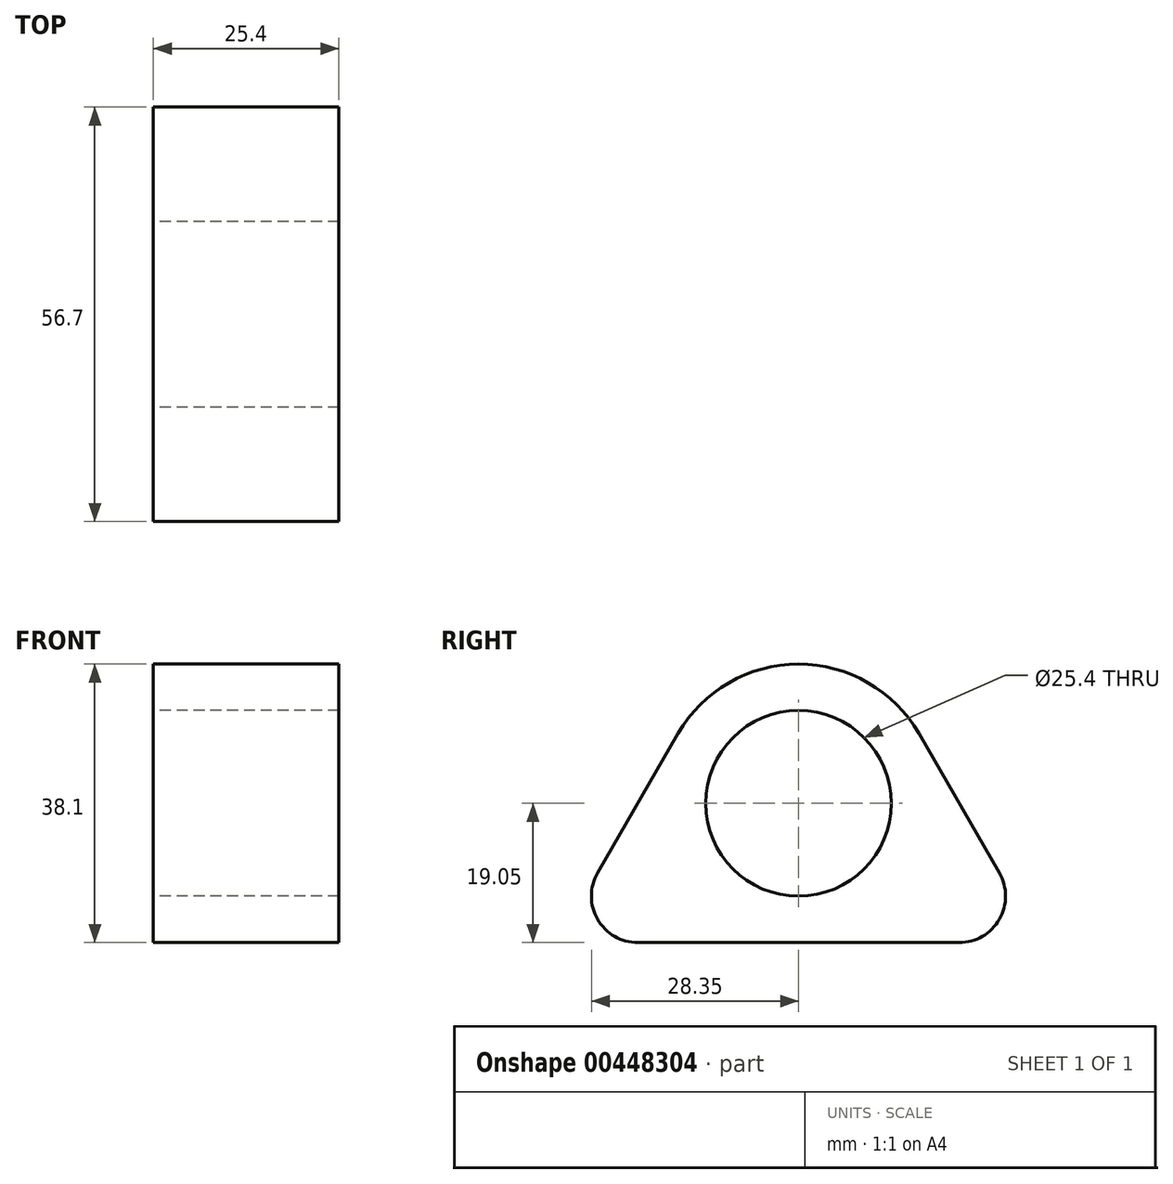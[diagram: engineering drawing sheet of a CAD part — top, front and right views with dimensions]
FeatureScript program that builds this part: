
annotation { "Feature Type Name" : "Feature", "Feature Type Description" : "" }
export const myFeature = defineFeature(function(context is Context, id is Id, definition is map)
    precondition{}
    {
        {
            var Q0;
            Q0=qCreatedBy(makeId("Right.planeOp"),FACE);
            var sketch = newSketch(context, id + "F0", { "sketchPlane" : qUnion([Q0])});
            skCircle(sketch, "E0", {"center": v(0, 0) * mm, "radius": 12.7 * mm});
            skCircle(sketch, "E1", {"center": v(0, 0) * mm, "radius": 19.05 * mm});
            skLineSegment(sketch, "E2", {"start": v(0, -19.05) * mm, "end": v(22, -19.05) * mm});
            skLineSegment(sketch, "E3", {"start": v(27.5, -9.52) * mm, "end": v(16.5, 9.53) * mm});
            skPoint(sketch, "E4.visualSharp", {"position": v(33, -19.05) * mm});
            skArc(sketch, "E4.filletArc", {"start": v(22, -19.05) * mm, "mid": v(27.5, -15.88) * mm, "end": v(27.5, -9.52) * mm});
            skLineSegment(sketch, "E5.MirrorCS", {"start": v(-27.5, -9.52) * mm, "end": v(-16.5, 9.53) * mm});
            skArc(sketch, "E6.MirrorCS", {"start": v(-22, -19.05) * mm, "mid": v(-27.5, -15.88) * mm, "end": v(-27.5, -9.52) * mm});
            skLineSegment(sketch, "E7.MirrorCS", {"start": v(0, -19.05) * mm, "end": v(-22, -19.05) * mm});
            skSolve(sketch);
        }
        {
            var Q0;
            Q0=makeQuery(id+"F0.imprint","IMPRINT",FACE,{"disambiguationData":[TD([[makeQuery(id+"F0.imprint","IMPRINT",EDGE,{"derivedFrom":sQuery(id+"F0.wireOp",EDGE,"E0")}),-1.0]])]});
            var Q1;
            {var subQ0=sQuery(id+"F0.wireOp",EDGE,"E2");Q1=makeQuery(id+"F0.imprint","IMPRINT",FACE,{"disambiguationData":[TD([[makeQuery(id+"F0.imprint","IMPRINT",EDGE,{"derivedFrom":subQ0}),1.0]])]});}
            var Q2;
            {var subQ2=sQuery(id+"F0.wireOp",EDGE,"E5.MirrorCS");Q2=makeQuery(id+"F0.imprint","IMPRINT",FACE,{"disambiguationData":[TD([[makeQuery(id+"F0.imprint","IMPRINT",EDGE,{"derivedFrom":subQ2}),-1.0]])]});}
            extrude(context, id + "F1", {"entities" : qUnion([Q0, Q1, Q2]), "depth" : 25.4 * mm});
        }
    });
